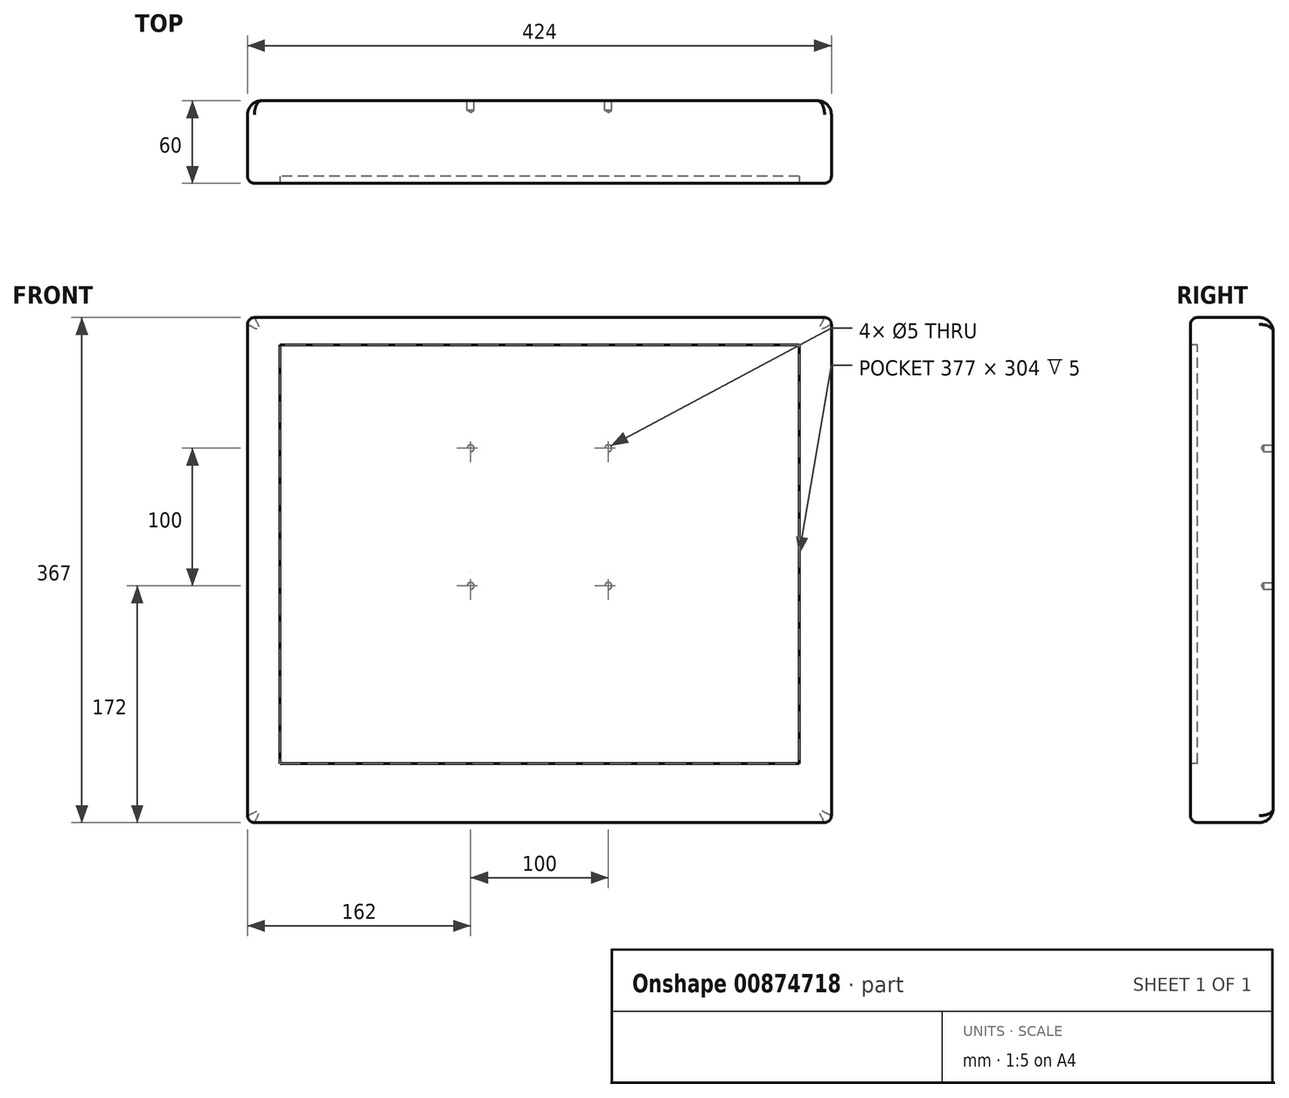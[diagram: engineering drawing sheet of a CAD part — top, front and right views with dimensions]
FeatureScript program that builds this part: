
annotation { "Feature Type Name" : "Feature", "Feature Type Description" : "" }
export const myFeature = defineFeature(function(context is Context, id is Id, definition is map)
    precondition{}
    {
        {
            var Q0;
            Q0=qCreatedBy(makeId("Front.planeOp"),FACE);
            var sketch = newSketch(context, id + "F0", { "sketchPlane" : qUnion([Q0])});
            skLineSegment(sketch, "E0.bottom", {"start": v(188.5, 178.27) * mm, "end": v(-188.5, 178.27) * mm});
            skLineSegment(sketch, "E0.top", {"start": v(188.5, 482.27) * mm, "end": v(-188.5, 482.27) * mm});
            skLineSegment(sketch, "E0.left", {"start": v(188.5, 178.27) * mm, "end": v(188.5, 482.27) * mm});
            skLineSegment(sketch, "E0.right", {"start": v(-188.5, 178.27) * mm, "end": v(-188.5, 482.27) * mm});
            skPoint(sketch, "E0.middle", {"position": v(0, 330.27) * mm});
            skLineSegment(sketch, "E1.bottom", {"start": v(-212, 502.27) * mm, "end": v(212, 502.27) * mm});
            skLineSegment(sketch, "E1.top", {"start": v(-212, 135.27) * mm, "end": v(212, 135.27) * mm});
            skLineSegment(sketch, "E1.left", {"start": v(-212, 502.27) * mm, "end": v(-212, 135.27) * mm});
            skLineSegment(sketch, "E1.right", {"start": v(212, 502.27) * mm, "end": v(212, 135.27) * mm});
            skPoint(sketch, "E2", {"position": v(0, 502.27) * mm});
            skSolve(sketch);
        }
        {
            var Q0;
            Q0=makeQuery(id+"F0.imprint","IMPRINT",FACE,{"disambiguationData":[TD([[makeQuery(id+"F0.imprint","IMPRINT",EDGE,{"derivedFrom":sQuery(id+"F0.wireOp",EDGE,"E0.bottom")}),1.0]])]});
            extrude(context, id + "F1", {"entities" : qUnion([Q0]), "oppositeDirection" : true, "depth" : 55 * mm, "offsetDistance" : 25 * mm, "hasSecondDirection" : true, "secondDirectionOppositeDirection" : false, "secondDirectionDepth" : 5 * mm});
        }
        {
            var Q0;
            Q0=makeQuery(id+"F0.imprint","IMPRINT",FACE,{"disambiguationData":[TD([[makeQuery(id+"F0.imprint","IMPRINT",EDGE,{"derivedFrom":sQuery(id+"F0.wireOp",EDGE,"E0.bottom")}),-1.0]])]});
            extrude(context, id + "F2", {"entities" : qUnion([Q0]), "oppositeDirection" : true, "depth" : 5 * mm, "offsetDistance" : 25 * mm});
        }
        {
            var Q0;
            Q0=makeQuery(id+"F0.imprint","IMPRINT",FACE,{"disambiguationData":[TD([[makeQuery(id+"F0.imprint","IMPRINT",EDGE,{"derivedFrom":sQuery(id+"F0.wireOp",EDGE,"E0.bottom")}),-1.0]])]});
            extrude(context, id + "F3", {"entities" : qUnion([Q0]), "operationType" : NewBodyOperationType.ADD, "oppositeDirection" : true, "depth" : 55 * mm, "offsetDistance" : 25 * mm});
        }
        {
            var Q0;
            {var subQ0=sQuery(id+"F0.wireOp",EDGE,"E0.right");var subQ1=sQuery(id+"F0.wireOp",EDGE,"E0.left");var subQ2=sQuery(id+"F0.wireOp",EDGE,"E0.top");var subQ3=sQuery(id+"F0.wireOp",EDGE,"E0.bottom");Q0=makeQuery(id+"F3.boolean.opBoolean","MERGE",FACE,{"derivedFrom":[makeQuery(id+"F1.opExtrude","CAP_FACE",FACE,{"disambiguationData":[OSD([subQ3,subQ2,subQ1,subQ0,sQuery(id+"F0.wireOp",EDGE,"E1.bottom"),sQuery(id+"F0.wireOp",EDGE,"E1.top"),sQuery(id+"F0.wireOp",EDGE,"E1.left"),sQuery(id+"F0.wireOp",EDGE,"E1.right")])],"isStart":false}),makeQuery(id+"F3.opExtrude","CAP_FACE",FACE,{"disambiguationData":[OSD([subQ3,subQ2,subQ1,subQ0])],"isStart":false})]});}
            var sketch = newSketch(context, id + "F4", { "sketchPlane" : qUnion([Q0])});
            skLineSegment(sketch, "E3.bottom", {"start": v(50, 407.27) * mm, "end": v(-50, 407.27) * mm, "construction": true});
            skLineSegment(sketch, "E3.top", {"start": v(50, 307.27) * mm, "end": v(-50, 307.27) * mm, "construction": true});
            skLineSegment(sketch, "E3.left", {"start": v(50, 407.27) * mm, "end": v(50, 307.27) * mm, "construction": true});
            skLineSegment(sketch, "E3.right", {"start": v(-50, 407.27) * mm, "end": v(-50, 307.27) * mm, "construction": true});
            skPoint(sketch, "E3.middle", {"position": v(0, 357.27) * mm});
            skSolve(sketch);
        }
        {
            var Q0;
            Q0=sQuery(id+"F4.wireOp",VERTEX,"E3.bottom.end");
            var Q1;
            Q1=sQuery(id+"F4.wireOp",VERTEX,"E3.top.end");
            var Q2;
            Q2=sQuery(id+"F4.wireOp",VERTEX,"E3.top.start");
            var Q3;
            Q3=sQuery(id+"F4.wireOp",VERTEX,"E3.bottom.start");
            var Q4;
            Q4=makeQuery(id+"F1.opExtrude","SWEPT_BODY",BODY,{"disambiguationData":[OSD([sQuery(id+"F0.wireOp",EDGE,"E0.bottom"),sQuery(id+"F0.wireOp",EDGE,"E0.top"),sQuery(id+"F0.wireOp",EDGE,"E0.left"),sQuery(id+"F0.wireOp",EDGE,"E0.right"),sQuery(id+"F0.wireOp",EDGE,"E1.bottom"),sQuery(id+"F0.wireOp",EDGE,"E1.top"),sQuery(id+"F0.wireOp",EDGE,"E1.left"),sQuery(id+"F0.wireOp",EDGE,"E1.right")])]});
            hole(context, id + "F5", {"style" : HoleStyle.SIMPLE, "endStyle" : HoleEndStyle.BLIND, "holeDiameter" : 5 * mm, "majorDiameter" : 5 * mm, "holeDepth" : 7 * mm, "isTappedThrough" : true, "tappedDepth" : 2 * mm, "tapClearance" : 3, "locations" : qUnion([Q0, Q1, Q2, Q3]), "scope" : qUnion([Q4])});
        }
        {
            var Q0;
            Q0=makeQuery(id+"F1.opExtrude","CAP_EDGE",EDGE,{"disambiguationData":[OSD([sQuery(id+"F0.wireOp",EDGE,"E1.top")])],"isStart":false});
            var Q1;
            Q1=makeQuery(id+"F1.opExtrude","CAP_EDGE",EDGE,{"disambiguationData":[OSD([sQuery(id+"F0.wireOp",EDGE,"E1.right")])],"isStart":false});
            var Q2;
            Q2=makeQuery(id+"F1.opExtrude","CAP_EDGE",EDGE,{"disambiguationData":[OSD([sQuery(id+"F0.wireOp",EDGE,"E1.bottom")])],"isStart":false});
            var Q3;
            Q3=makeQuery(id+"F1.opExtrude","CAP_EDGE",EDGE,{"disambiguationData":[OSD([sQuery(id+"F0.wireOp",EDGE,"E1.left")])],"isStart":false});
            fillet(context, id + "F6", {"entities" : qUnion([Q0, Q1, Q2, Q3]), "radius" : 10 * mm, "tangentPropagation" : true, "allowEdgeOverflow" : false});
        }
        {
            var Q0;
            Q0=makeQuery(id+"F1.opExtrude","SWEPT_EDGE",EDGE,{"disambiguationData":[OSD([sQuery(id+"F0.wireOp",EDGE,"E1.bottom"),sQuery(id+"F0.wireOp",EDGE,"E1.right")])]});
            var Q1;
            Q1=makeQuery(id+"F1.opExtrude","SWEPT_EDGE",EDGE,{"disambiguationData":[OSD([sQuery(id+"F0.wireOp",EDGE,"E1.bottom"),sQuery(id+"F0.wireOp",EDGE,"E1.left")])]});
            var Q2;
            Q2=makeQuery(id+"F1.opExtrude","SWEPT_EDGE",EDGE,{"disambiguationData":[OSD([sQuery(id+"F0.wireOp",EDGE,"E1.top"),sQuery(id+"F0.wireOp",EDGE,"E1.right")])]});
            var Q3;
            Q3=makeQuery(id+"F1.opExtrude","SWEPT_EDGE",EDGE,{"disambiguationData":[OSD([sQuery(id+"F0.wireOp",EDGE,"E1.top"),sQuery(id+"F0.wireOp",EDGE,"E1.left")])]});
            fillet(context, id + "F7", {"entities" : qUnion([Q0, Q1, Q2, Q3]), "radius" : 5 * mm, "tangentPropagation" : true, "allowEdgeOverflow" : false});
        }
        {
            var Q0;
            Q0=makeQuery(id+"F1.opExtrude","CAP_EDGE",EDGE,{"disambiguationData":[OSD([sQuery(id+"F0.wireOp",EDGE,"E1.left")])],"isStart":true});
            fillet(context, id + "F8", {"entities" : qUnion([Q0]), "radius" : 5 * mm, "tangentPropagation" : true, "allowEdgeOverflow" : false});
        }
    });
